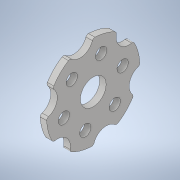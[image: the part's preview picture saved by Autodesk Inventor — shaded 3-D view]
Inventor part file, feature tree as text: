
AUTODESK INVENTOR PART (.ipt)
format: ipt  version: 2021 (Build 250183000, 183)  size: 173,056 bytes
history: native  units: in
note: dims shown in document units (in); Inventor stores cm internally (conversion verified against a paired STEP export)
features: extrude x1, fillet x1, sketch x1
ambient origin geometry x8: Origin, YZ Plane, XZ Plane, XY Plane, X Axis, Y Axis, Z Axis, Center Point
bodies: Solid1 (feature_tree)
feature tree (3):
  extrude  "Extrusion1"  Depth=0.125in
  fillet  "Fillet1"  Radius=0.55in
  sketch  "Sketch1"  dims[d0=4.517in d1=2.952in d2=0.55in d3=45.0deg d4=2.3622in d6=360.0deg d8=1.25in d12=1.25in d16=15.0deg d17=2.3622in d19=360.0deg d21=0.3125in d22=0.0in d23=0.125in]
